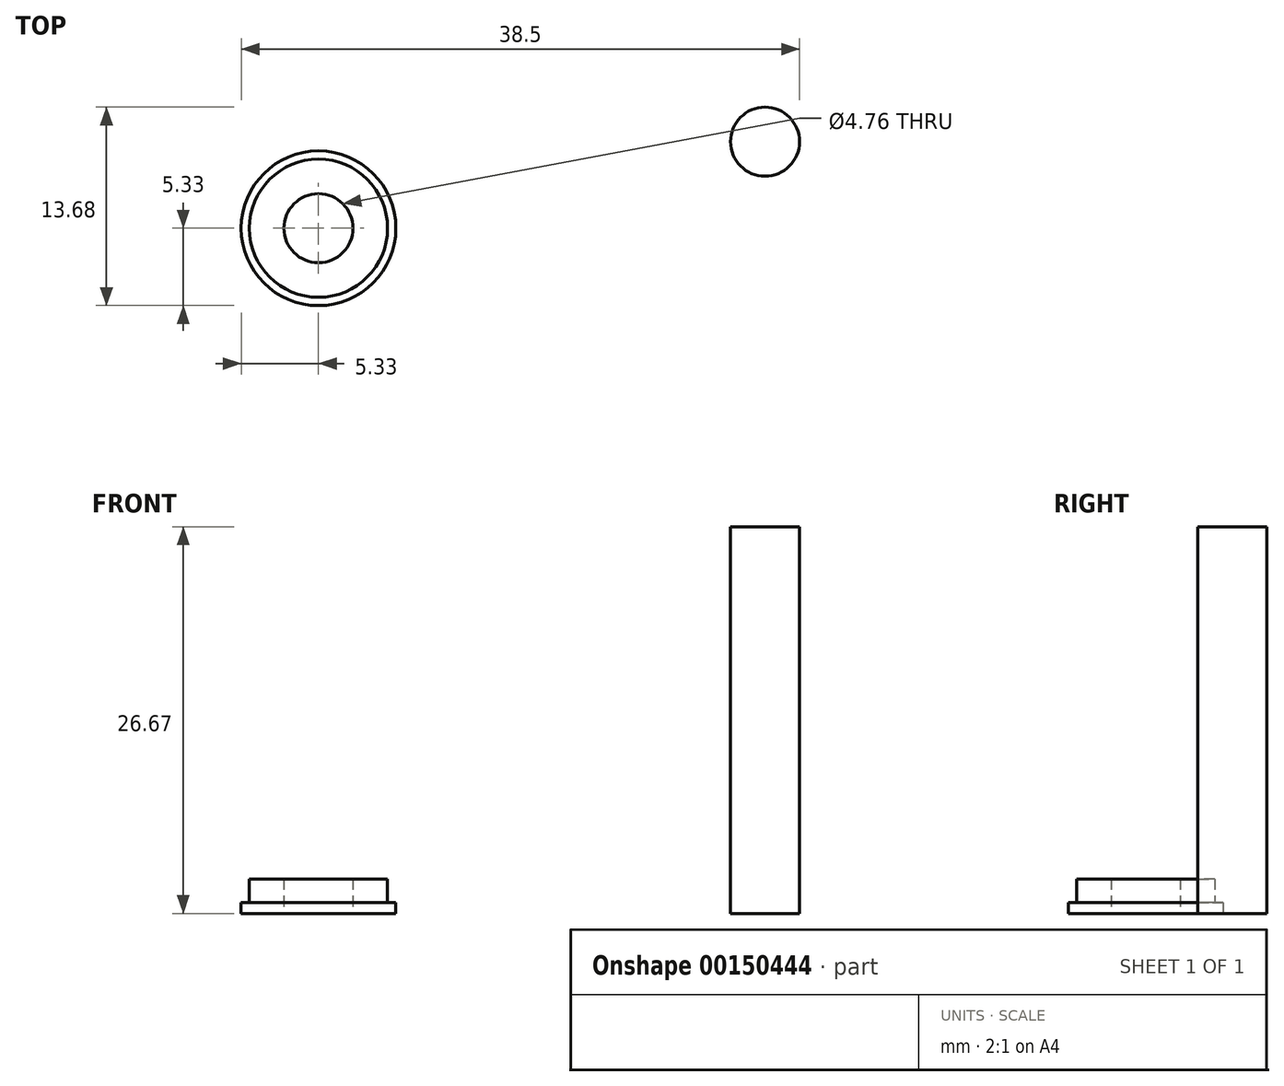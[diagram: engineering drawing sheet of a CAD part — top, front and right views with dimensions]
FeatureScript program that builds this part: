
annotation { "Feature Type Name" : "Feature", "Feature Type Description" : "" }
export const myFeature = defineFeature(function(context is Context, id is Id, definition is map)
    precondition{}
    {
        {
            var Q0;
            Q0=qCreatedBy(makeId("Top.planeOp"),FACE);
            var sketch = newSketch(context, id + "F0", { "sketchPlane" : qUnion([Q0])});
            skCircle(sketch, "E0", {"center": v(0, 0) * mm, "radius": 5.33 * mm});
            skCircle(sketch, "E1", {"center": v(0, 0) * mm, "radius": 2.38 * mm});
            skSolve(sketch);
        }
        {
            var Q0;
            Q0 = qSketchRegion(id + "F0", true);
            extrude(context, id + "F1", {"entities" : qUnion([Q0]), "depth" : 0.76 * mm});
        }
        {
            var Q0;
            Q0=qCreatedBy(makeId("Top.planeOp"),FACE);
            var sketch = newSketch(context, id + "F2", { "sketchPlane" : qUnion([Q0])});
            skCircle(sketch, "E2", {"center": v(0, 0) * mm, "radius": 4.76 * mm});
            skCircle(sketch, "E3", {"center": v(0, 0) * mm, "radius": 2.38 * mm});
            skSolve(sketch);
        }
        {
            var Q0;
            Q0 = qSketchRegion(id + "F2", true);
            extrude(context, id + "F3", {"entities" : qUnion([Q0]), "operationType" : NewBodyOperationType.ADD, "depth" : 2.37 * mm});
        }
        {
            var Q0;
            Q0=qCreatedBy(makeId("Top.planeOp"),FACE);
            var sketch = newSketch(context, id + "F4", { "sketchPlane" : qUnion([Q0])});
            skCircle(sketch, "E4", {"center": v(30.8, 5.97) * mm, "radius": 2.38 * mm});
            skSolve(sketch);
        }
        {
            var Q0;
            Q0 = qSketchRegion(id + "F4", true);
            extrude(context, id + "F5", {"entities" : qUnion([Q0]), "depth" : 26.67 * mm});
        }
    });
